MODEL slx_6dc7536a5b94
CONFIG AbsTol = auto
CONFIG EnableMultiTasking = off
CONFIG FixedStep = auto
CONFIG InitFcn = Wc = 1;

T = 0.001;

Kp = 0.8;
Ki = 1.2;
CONFIG MaxStep = auto
CONFIG MinStep = auto
CONFIG RelTol = 1e-3
CONFIG SampleTimeConstraint = Unconstrained
CONFIG SolverName = VariableStepAuto
CONFIG StartTime = 0.0
CONFIG StopTime = 10.0
BLOCK [Sum] Add1
  IconShape = rectangular
  Inputs = ++++
BLOCK [CCaller] C Caller3
  FunctionName = PLL_SingleLoop
  PortSpecificationStruct = %)30     .    F 4   8    (     @         %    "     ,    !     0         %  0 "0    $    _    07)G3F%M90  4&]R=$YA;64 4V-O<&4     26YD97@     5'EP90      4VEZ90      27-';&]B86P   X    X    !@    @    $          4    (     0    4    !         !     %    :6YP=70    .    .     8    (    !          %    "     $    %     0         0    !0   &EN<'5T    #@   #@    &    "     0         !0    @    !    !0...<+1522ch>
BLOCK [DataTypeConversion] Data Type Conversion3
  OutDataTypeStr = single
  RndMeth = Floor
  SaturateOnIntegerOverflow = off
BLOCK [Delay] Delay2
  DelayLength = 1
  InputPortMap = u0
  NameLocation = top
BLOCK [DiscreteTransferFcn] Discrete Transfer Fcn16
  CloseFcn = dspblkCoreblockFVToolHelper(gcbh,'close');
  CopyFcn = dspblkCoreblockFVToolHelper(gcbh,'copy');
  DeleteFcn = dspblkCoreblockFVToolHelper(gcbh,'close');
  Denominator = [2 -2]
  InputPortMap = u0
  LoadFcn = dspblkCoreblockFVToolHelper(gcbh,'load');
  ModelCloseFcn = dspblkCoreblockFVToolHelper(gcbh,'close');
  Numerator = [(2*Kp+Ki*T) -2*Kp+Ki*T]
  PostSaveFcn = dspblkCoreblockFVToolHelper(gcbh,'postsave');
  PreSaveFcn = dspblkCoreblockFVToolHelper(gcbh,'presave');
BLOCK [DiscreteTransferFcn] Discrete Transfer Fcn17
  CloseFcn = dspblkCoreblockFVToolHelper(gcbh,'close');
  CopyFcn = dspblkCoreblockFVToolHelper(gcbh,'copy');
  DeleteFcn = dspblkCoreblockFVToolHelper(gcbh,'close');
  Denominator = [2 -2]
  InputPortMap = u0
  LoadFcn = dspblkCoreblockFVToolHelper(gcbh,'load');
  ModelCloseFcn = dspblkCoreblockFVToolHelper(gcbh,'close');
  Numerator = [T T]
  PostSaveFcn = dspblkCoreblockFVToolHelper(gcbh,'postsave');
  PreSaveFcn = dspblkCoreblockFVToolHelper(gcbh,'presave');
BLOCK [DiscreteTransferFcn] Discrete Transfer Fcn18
  CloseFcn = dspblkCoreblockFVToolHelper(gcbh,'close');
  CopyFcn = dspblkCoreblockFVToolHelper(gcbh,'copy');
  DeleteFcn = dspblkCoreblockFVToolHelper(gcbh,'close');
  Denominator = [(2+T*Wc) -2+T*Wc]
  InputPortMap = u0
  LoadFcn = dspblkCoreblockFVToolHelper(gcbh,'load');
  ModelCloseFcn = dspblkCoreblockFVToolHelper(gcbh,'close');
  Numerator = [T*Wc T*Wc]
  PostSaveFcn = dspblkCoreblockFVToolHelper(gcbh,'postsave');
  PreSaveFcn = dspblkCoreblockFVToolHelper(gcbh,'presave');
BLOCK [From] From10
  GotoTag = Run
BLOCK [From] From11
  GotoTag = Run
BLOCK [From] From12
  GotoTag = Run
BLOCK [From] From13
  GotoTag = Run
BLOCK [Gain] Gain19
  Gain = Kp
BLOCK [Gain] Gain20
  Gain = Ki
BLOCK [Goto] Goto3
  GotoTag = Run
BLOCK [Reference] Ramp1  REF=simulink/Sources/Ramp
  SourceBlock = simulink/Sources/Ramp
  SourceType = Ramp
BLOCK [Scope] Scope12
  ActiveDisplayYMaximum = 11.267329216003418
  ActiveDisplayYMinimum = -1.251925468444824
  DataLoggingVariableName = ScopeData13
  Floating = off
  GraphicalSettings = {"Style":{"BackgroundColor":[0.12941176470588237,0.12941176470588237,0.12941176470588237],"AxesColor":[0.07058823529411765,0.07058823529411765,0.07058823529411765],"LabelsColor":[0.8509803921568627,0.8509803921568627,0.8509803921568627],"PreserveColors":false,"Visible":[true,true],"LineStyle":["-","-"],"LineWidth":[1.5,1.5],"BarWidth":[0.9,0.9],"LineColor":["auto","auto"],"LineFaceAlpha":[1,1],"Li...<+2126ch>
  MultipleDisplayCache = [{"MaxYLimMag":11.267329216003418,"MaxYLimReal":11.267329216003418,"MinYLimMag":0,"MinYLimReal":-1.251925468444824,"PlotAsMagnitudePhase":false,"ShowGrid":true,"ShowLegend":true,"Title":"%<SignalLabel>","YLabel":""}]
  NumInputPorts = 2
  ScopeFrameLocation = window
  ShowLegend = on
  WasSavedAsWebScope = on
  WindowPosition = [531.000000,371.000000,560.000000,420.000000,]
BLOCK [Scope] Scope9
  ActiveDisplayYMaximum = 11.854858515541672
  ActiveDisplayYMinimum = -1.8025038091260754
  DataLoggingVariableName = ScopeData10
  Floating = off
  GraphicalSettings = {"Style":{"BackgroundColor":[0.12941176470588237,0.12941176470588237,0.12941176470588237],"AxesColor":[0.07058823529411765,0.07058823529411765,0.07058823529411765],"LabelsColor":[0.8509803921568627,0.8509803921568627,0.8509803921568627],"PreserveColors":false,"Visible":[true,true,true,true,true,true,true],"LineStyle":["-","-","-","-","-","-","-"],"LineWidth":[1.5,1.5,1.5,1.5,1.5,1.5,1.5],"BarWidth...<+2767ch>
  MultipleDisplayCache = [{"MaxYLimMag":11.854858515541672,"MaxYLimReal":11.854858515541672,"MinYLimMag":0,"MinYLimReal":-1.8025038091260754,"PlotAsMagnitudePhase":false,"ShowGrid":true,"ShowLegend":true,"Title":"%<SignalLabel>","YLabel":""}]
  NumInputPorts = 7
  ScopeFrameLocation = window
  ShowLegend = on
  WasSavedAsWebScope = on
  WindowPosition = [582.000000,356.000000,560.000000,420.000000,]
BLOCK [Sin] Sine Wave6
  Amplitude = 0.3
  Frequency = 80
  SampleTime = 0
BLOCK [Sin] Sine Wave7
  Amplitude = 0.2
  Frequency = 300
  SampleTime = 0
BLOCK [Sin] Sine Wave8
  Amplitude = 0.003
  Frequency = 1000
  SampleTime = 0
BLOCK [Sum] Sum10
  Inputs = |+-
BLOCK [Sum] Sum13
  Inputs = |+-
BLOCK [Sum] Sum9
  Inputs = ++|
BLOCK [TransferFcn] Transfer Fcn16
  Denominator = [1 0]
BLOCK [TransferFcn] Transfer Fcn17
  Denominator = [1 0]
BLOCK [TransferFcn] Transfer Fcn20
  Denominator = [1 1]
BLOCK [ZeroOrderHold] Zero-Order Hold10
  SampleTime = 0.001
BLOCK [ZeroOrderHold] Zero-Order Hold9
  SampleTime = 0.001
LINE Add1:1 -> Goto3:1
LINE C Caller3:1 -> Scope12:1
LINE C Caller3:1 -> Scope9:6
LINE C Caller3:2 -> Scope12:2
LINE C Caller3:2 -> Scope9:7
LINE Data Type Conversion3:1 -> C Caller3:1
LINE Delay2:1 -> Sum13:2
LINE Discrete Transfer Fcn16:1 -> Discrete Transfer Fcn17:1
LINE Discrete Transfer Fcn16:1 -> Discrete Transfer Fcn18:1
LINE Discrete Transfer Fcn17:1 -> Delay2:1
LINE Discrete Transfer Fcn17:1 -> Scope9:5
LINE Discrete Transfer Fcn18:1 -> Scope9:4
LINE From10:1 -> Sum10:1
LINE From11:1 -> Scope9:1
LINE From12:1 -> Zero-Order Hold9:1
LINE From13:1 -> Zero-Order Hold10:1
LINE Gain19:1 -> Sum9:2
LINE Gain20:1 -> Transfer Fcn16:1
LINE Ramp1:1 -> Add1:1
LINE Sine Wave6:1 -> Add1:2
LINE Sine Wave7:1 -> Add1:3
LINE Sine Wave8:1 -> Add1:4
LINE Sum10:1 -> Gain19:1
LINE Sum10:1 -> Gain20:1
LINE Sum13:1 -> Discrete Transfer Fcn16:1
LINE Sum9:1 -> Transfer Fcn17:1
LINE Sum9:1 -> Transfer Fcn20:1
LINE Transfer Fcn16:1 -> Sum9:1
LINE Transfer Fcn17:1 -> Scope9:3
LINE Transfer Fcn17:1 -> Sum10:2
LINE Transfer Fcn20:1 -> Scope9:2
LINE Zero-Order Hold10:1 -> Data Type Conversion3:1
LINE Zero-Order Hold9:1 -> Sum13:1
